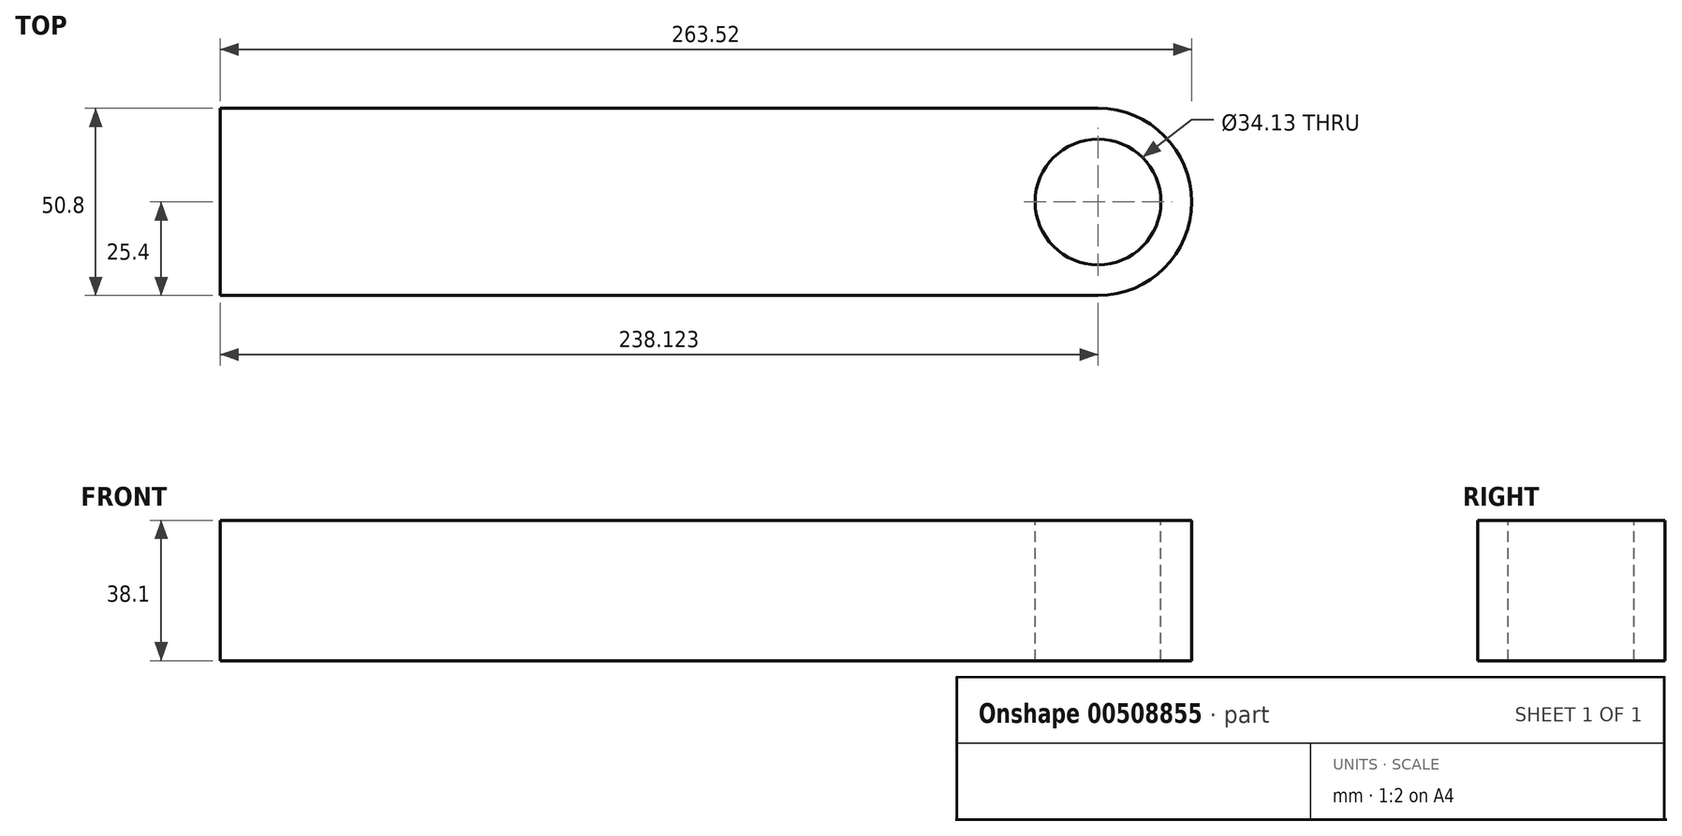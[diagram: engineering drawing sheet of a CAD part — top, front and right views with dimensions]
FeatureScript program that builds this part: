
annotation { "Feature Type Name" : "Feature", "Feature Type Description" : "" }
export const myFeature = defineFeature(function(context is Context, id is Id, definition is map)
    precondition{}
    {
        {
            var Q0;
            Q0=qCreatedBy(makeId("Top.planeOp"),FACE);
            var sketch = newSketch(context, id + "F0", { "sketchPlane" : qUnion([Q0])});
            skLineSegment(sketch, "E0.bottom", {"start": v(119.06, 25.4) * mm, "end": v(-119.06, 25.4) * mm});
            skLineSegment(sketch, "E0.top", {"start": v(119.06, -25.4) * mm, "end": v(-119.06, -25.4) * mm});
            skLineSegment(sketch, "E0.left", {"start": v(119.06, 25.4) * mm, "end": v(119.06, -25.4) * mm, "construction": true});
            skLineSegment(sketch, "E0.right", {"start": v(-119.06, 25.4) * mm, "end": v(-119.06, -25.4) * mm});
            skPoint(sketch, "E0.middle", {"position": v(0, 0) * mm});
            skArc(sketch, "E1", {"start": v(119.06, -25.4) * mm, "mid": v(144.46, 0) * mm, "end": v(119.06, 25.4) * mm});
            skSolve(sketch);
        }
        {
            var Q0;
            Q0=makeQuery(id+"F0.imprint","IMPRINT",FACE,{"disambiguationData":[TD([[makeQuery(id+"F0.imprint","IMPRINT",EDGE,{"derivedFrom":sQuery(id+"F0.wireOp",EDGE,"E0.bottom")}),1.0]])]});
            extrude(context, id + "F1", {"entities" : qUnion([Q0]), "depth" : 38.1 * mm});
        }
        {
            var Q0;
            Q0=makeQuery(id+"F1.opExtrude","CAP_FACE",FACE,{"disambiguationData":[OSD([sQuery(id+"F0.wireOp",EDGE,"E0.bottom"),sQuery(id+"F0.wireOp",EDGE,"E0.top"),sQuery(id+"F0.wireOp",EDGE,"E0.right"),sQuery(id+"F0.wireOp",EDGE,"E1")])],"isStart":false});
            var sketch = newSketch(context, id + "F2", { "sketchPlane" : qUnion([Q0])});
            skPoint(sketch, "E2", {"position": v(119.06, 0) * mm});
            skSolve(sketch);
        }
        {
            var Q0;
            Q0=sQuery(id+"F2.wireOp",VERTEX,"E2");
            var Q1;
            Q1=makeQuery(id+"F1.opExtrude","SWEPT_BODY",BODY,{"disambiguationData":[OSD([sQuery(id+"F0.wireOp",EDGE,"E0.bottom"),sQuery(id+"F0.wireOp",EDGE,"E0.top"),sQuery(id+"F0.wireOp",EDGE,"E0.right"),sQuery(id+"F0.wireOp",EDGE,"E1")])]});
            hole(context, id + "F3", {"style" : HoleStyle.SIMPLE, "endStyle" : HoleEndStyle.THROUGH, "standardTappedOrClearance" : lookupTablePath({ "standard" : "ANSI", "engagement" : "75%", "pitch" : "6 tpi", "size" : "1 1/2", "type" : "Tapped" }), "standardBlindInLast" : lookupTablePath({ "standard" : "ANSI", "engagement" : "75%", "pitch" : "6 tpi", "size" : "1 1/2", "type" : "Tapped" }), "holeDiameter" : 34.13 * mm, "showTappedDepth" : true, "isTappedThrough" : true, "tappedDepth" : 31.76 * mm, "tapClearance" : 3, "locations" : qUnion([Q0]), "scope" : qUnion([Q1]), "majorDiameter" : 38.1 * mm});
        }
    });
